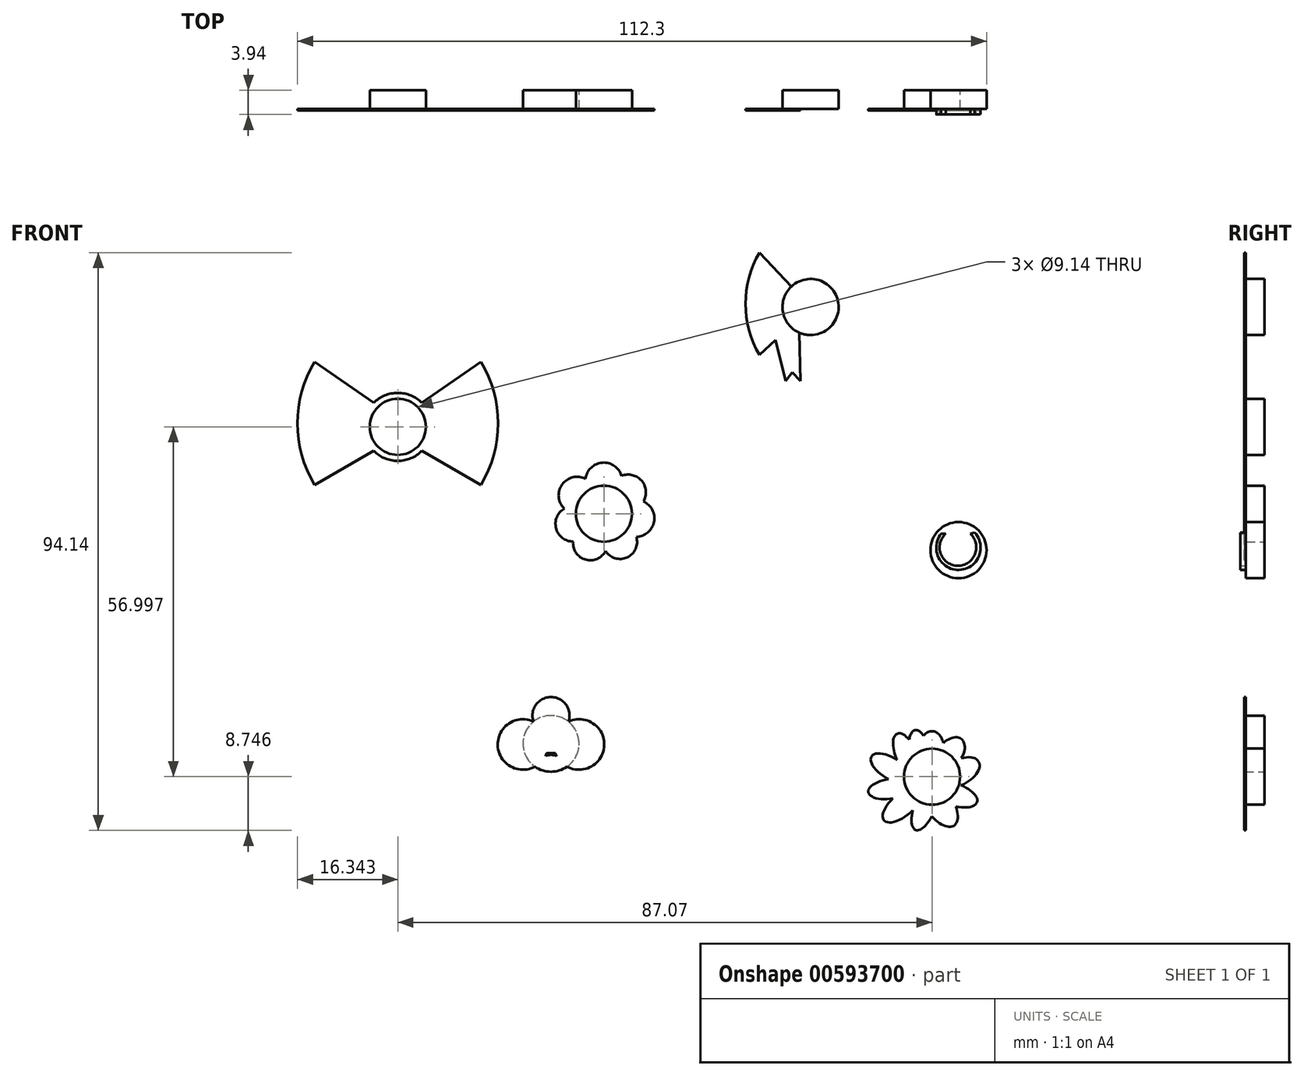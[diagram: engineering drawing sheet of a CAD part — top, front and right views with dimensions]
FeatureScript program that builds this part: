
annotation { "Feature Type Name" : "Feature", "Feature Type Description" : "" }
export const myFeature = defineFeature(function(context is Context, id is Id, definition is map)
    precondition{}
    {
        {
            var Q0;
            Q0=qCreatedBy(makeId("Front.planeOp"),FACE);
            var sketch = newSketch(context, id + "F0", { "sketchPlane" : qUnion([Q0])});
            skCircle(sketch, "E0", {"center": v(-50.12, 43.15) * mm, "radius": 4.57 * mm});
            skCircle(sketch, "E1", {"center": v(-16.53, 29) * mm, "radius": 4.57 * mm});
            skCircle(sketch, "E2", {"center": v(41.26, 23.07) * mm, "radius": 4.57 * mm});
            skCircle(sketch, "E3", {"center": v(17.15, 62.68) * mm, "radius": 4.57 * mm});
            skCircle(sketch, "E4", {"center": v(-25.15, -8.45) * mm, "radius": 4.57 * mm});
            skCircle(sketch, "E5", {"center": v(36.95, -13.84) * mm, "radius": 4.57 * mm});
            skSolve(sketch);
        }
        {
            var Q0;
            Q0=makeQuery(id+"F0.imprint","IMPRINT",FACE,{"disambiguationData":[TD([[makeQuery(id+"F0.imprint","IMPRINT",EDGE,{"derivedFrom":sQuery(id+"F0.wireOp",EDGE,"E0")}),1.0]])]});
            var Q1;
            Q1=makeQuery(id+"F0.imprint","IMPRINT",FACE,{"disambiguationData":[TD([[makeQuery(id+"F0.imprint","IMPRINT",EDGE,{"derivedFrom":sQuery(id+"F0.wireOp",EDGE,"E1")}),1.0]])]});
            var Q2;
            Q2=makeQuery(id+"F0.imprint","IMPRINT",FACE,{"disambiguationData":[TD([[makeQuery(id+"F0.imprint","IMPRINT",EDGE,{"derivedFrom":sQuery(id+"F0.wireOp",EDGE,"E3")}),1.0]])]});
            var Q3;
            Q3=makeQuery(id+"F0.imprint","IMPRINT",FACE,{"disambiguationData":[TD([[makeQuery(id+"F0.imprint","IMPRINT",EDGE,{"derivedFrom":sQuery(id+"F0.wireOp",EDGE,"E2")}),1.0]])]});
            var Q4;
            Q4=makeQuery(id+"F0.imprint","IMPRINT",FACE,{"disambiguationData":[TD([[makeQuery(id+"F0.imprint","IMPRINT",EDGE,{"derivedFrom":sQuery(id+"F0.wireOp",EDGE,"E4")}),1.0]])]});
            var Q5;
            Q5=makeQuery(id+"F0.imprint","IMPRINT",FACE,{"disambiguationData":[TD([[makeQuery(id+"F0.imprint","IMPRINT",EDGE,{"derivedFrom":sQuery(id+"F0.wireOp",EDGE,"E5")}),1.0]])]});
            extrude(context, id + "F1", {"entities" : qUnion([Q0, Q1, Q2, Q3, Q4, Q5]), "depth" : 3.05 * mm, "offsetDistance" : 25.4 * mm});
        }
        {
            var Q0;
            Q0=makeQuery(id+"F1.opExtrude","CAP_FACE",FACE,{"disambiguationData":[OSD([sQuery(id+"F0.wireOp",EDGE,"E0")])],"isStart":false});
            var sketch = newSketch(context, id + "F2", { "sketchPlane" : qUnion([Q0])});
            skCircle(sketch, "E6", {"center": v(-50.12, 43.15) * mm, "radius": 5.54 * mm});
            skLineSegment(sketch, "E7", {"start": v(-46.2, 47.06) * mm, "end": v(-36.57, 53.77) * mm});
            skLineSegment(sketch, "E8", {"start": v(-46.2, 39.24) * mm, "end": v(-36.57, 33.68) * mm});
            skArc(sketch, "E9", {"start": v(-36.57, 33.68) * mm, "mid": v(-33.77, 43.73) * mm, "end": v(-36.57, 53.77) * mm});
            skLineSegment(sketch, "E10.MirrorCS", {"start": v(-54.04, 47.06) * mm, "end": v(-63.67, 53.77) * mm});
            skLineSegment(sketch, "E11.MirrorCS", {"start": v(-54.04, 39.24) * mm, "end": v(-63.67, 33.68) * mm});
            skArc(sketch, "E12.MirrorCS", {"start": v(-63.67, 33.68) * mm, "mid": v(-66.46, 43.73) * mm, "end": v(-63.67, 53.77) * mm});
            skSolve(sketch);
        }
        {
            var Q0;
            Q0=makeQuery(id+"F2.imprint","IMPRINT",FACE,{"disambiguationData":[TD([[makeQuery(id+"F2.imprint","IMPRINT",EDGE,{"derivedFrom":makeQuery(id+"F1.opExtrude","CAP_EDGE",EDGE,{"disambiguationData":[OSD([sQuery(id+"F0.wireOp",EDGE,"E0")])],"isStart":false})}),-1.0]])]});
            extrude(context, id + "F3", {"entities" : qUnion([Q0]), "depth" : 0.25 * mm, "offsetDistance" : 25.4 * mm});
        }
        {
            var Q0;
            {var subQ0=sQuery(id+"F2.wireOp",EDGE,"E10.MirrorCS");Q0=makeQuery(id+"F2.imprint","IMPRINT",FACE,{"disambiguationData":[TD([[makeQuery(id+"F2.imprint","IMPRINT",EDGE,{"derivedFrom":subQ0}),1.0]])]});}
            var Q1;
            {var subQ0=sQuery(id+"F2.wireOp",EDGE,"E7");Q1=makeQuery(id+"F2.imprint","IMPRINT",FACE,{"disambiguationData":[TD([[makeQuery(id+"F2.imprint","IMPRINT",EDGE,{"derivedFrom":subQ0}),-1.0]])]});}
            extrude(context, id + "F4", {"entities" : qUnion([Q0, Q1]), "operationType" : NewBodyOperationType.ADD, "depth" : 0.25 * mm, "offsetDistance" : 25.4 * mm});
        }
        {
            var Q0;
            Q0=makeQuery(id+"F1.opExtrude","CAP_FACE",FACE,{"disambiguationData":[OSD([sQuery(id+"F0.wireOp",EDGE,"E1")])],"isStart":false});
            var sketch = newSketch(context, id + "F5", { "sketchPlane" : qUnion([Q0])});
            skArc(sketch, "E13", {"start": v(-17.86, 31.63) * mm, "mid": v(-16.6, 31.33) * mm, "end": v(-15.32, 31.58) * mm});
            skArc(sketch, "E14", {"start": v(-19.53, 34.7) * mm, "mid": v(-23.34, 33.75) * mm, "end": v(-23, 29.83) * mm});
            skArc(sketch, "E15", {"start": v(-23, 29.83) * mm, "mid": v(-24.32, 26.6) * mm, "end": v(-21.54, 24.47) * mm});
            skArc(sketch, "E16", {"start": v(-21.54, 24.47) * mm, "mid": v(-19.54, 21.53) * mm, "end": v(-16.26, 22.93) * mm});
            skArc(sketch, "E17", {"start": v(-16.26, 22.93) * mm, "mid": v(-12.75, 21.89) * mm, "end": v(-11.24, 25.24) * mm});
            skArc(sketch, "E18", {"start": v(-11.24, 25.24) * mm, "mid": v(-8.37, 27.65) * mm, "end": v(-10.1, 30.99) * mm});
            skArc(sketch, "E19", {"start": v(-10.1, 30.99) * mm, "mid": v(-10.37, 34.36) * mm, "end": v(-13.66, 35.17) * mm});
            skArc(sketch, "E20.trimOffspring", {"start": v(-19.44, 29.32) * mm, "mid": v(-18.37, 30.28) * mm, "end": v(-17.86, 31.63) * mm});
            skArc(sketch, "E21.trimOffspring", {"start": v(-18.68, 27.01) * mm, "mid": v(-18.8, 28.25) * mm, "end": v(-19.44, 29.32) * mm});
            skPoint(sketch, "E22.center.orphan", {"position": v(-16.53, 29) * mm});
            skArc(sketch, "E23.trimOffspring", {"start": v(-16.38, 25.7) * mm, "mid": v(-17.37, 26.65) * mm, "end": v(-18.68, 27.01) * mm});
            skArc(sketch, "E24.trimOffspring", {"start": v(-14.13, 27.2) * mm, "mid": v(-15.45, 26.74) * mm, "end": v(-16.38, 25.7) * mm});
            skArc(sketch, "E25.trimOffspring", {"start": v(-13.83, 29.88) * mm, "mid": v(-14.3, 28.57) * mm, "end": v(-14.13, 27.2) * mm});
            skArc(sketch, "E26.trimOffspring", {"start": v(-15.32, 31.58) * mm, "mid": v(-14.75, 30.58) * mm, "end": v(-13.83, 29.88) * mm});
            skArc(sketch, "E27.trimOffspring", {"start": v(-13.66, 35.17) * mm, "mid": v(-16.78, 37.32) * mm, "end": v(-19.53, 34.7) * mm});
            skSolve(sketch);
        }
        {
            var Q0;
            Q0=makeQuery(id+"F5.imprint","IMPRINT",FACE,{"disambiguationData":[TD([[makeQuery(id+"F5.imprint","IMPRINT",EDGE,{"derivedFrom":sQuery(id+"F5.wireOp",EDGE,"E14")}),1.0]])]});
            extrude(context, id + "F6", {"entities" : qUnion([Q0]), "depth" : 0.25 * mm, "offsetDistance" : 25.4 * mm});
        }
        {
            var Q0;
            Q0=makeQuery(id+"F1.opExtrude","CAP_FACE",FACE,{"disambiguationData":[OSD([sQuery(id+"F0.wireOp",EDGE,"E3")])],"isStart":false});
            var sketch = newSketch(context, id + "F7", { "sketchPlane" : qUnion([Q0])});
            skLineSegment(sketch, "E28", {"start": v(17.15, 62.68) * mm, "end": v(8.82, 71.55) * mm});
            skLineSegment(sketch, "E29", {"start": v(17.15, 62.68) * mm, "end": v(15.24, 60.88) * mm});
            skArc(sketch, "E30", {"start": v(8.82, 71.55) * mm, "mid": v(6.56, 63.2) * mm, "end": v(8.82, 54.86) * mm});
            skLineSegment(sketch, "E31.MirrorCS", {"start": v(17.15, 62.68) * mm, "end": v(25.48, 71.55) * mm});
            skArc(sketch, "E32.MirrorCS", {"start": v(25.48, 71.55) * mm, "mid": v(27.74, 63.2) * mm, "end": v(25.48, 54.86) * mm});
            skLineSegment(sketch, "E33.MirrorCS", {"start": v(17.15, 62.68) * mm, "end": v(19.06, 60.88) * mm});
            skLineSegment(sketch, "E34", {"start": v(15.47, 50.66) * mm, "end": v(14.16, 52.05) * mm});
            skLineSegment(sketch, "E35", {"start": v(14.16, 52.05) * mm, "end": v(13.1, 50.66) * mm});
            skLineSegment(sketch, "E36", {"start": v(13.1, 50.66) * mm, "end": v(11.44, 57.32) * mm});
            skLineSegment(sketch, "E37", {"start": v(15.47, 50.66) * mm, "end": v(15.24, 60.88) * mm});
            skLineSegment(sketch, "E38.trimOffspring", {"start": v(11.44, 57.32) * mm, "end": v(8.82, 54.86) * mm});
            skLineSegment(sketch, "E39.MirrorCS", {"start": v(21.2, 50.66) * mm, "end": v(22.86, 57.32) * mm});
            skLineSegment(sketch, "E40.MirrorCS", {"start": v(18.83, 50.66) * mm, "end": v(19.06, 60.88) * mm});
            skLineSegment(sketch, "E41.MirrorCS", {"start": v(18.83, 50.66) * mm, "end": v(20.14, 52.05) * mm});
            skLineSegment(sketch, "E42.MirrorCS", {"start": v(20.14, 52.05) * mm, "end": v(21.2, 50.66) * mm});
            skLineSegment(sketch, "E43.trimOffspring", {"start": v(22.86, 57.32) * mm, "end": v(25.48, 54.86) * mm});
            skSolve(sketch);
        }
        {
            var Q0;
            {var subQ0=sQuery(id+"F7.wireOp",EDGE,"E30");Q0=makeQuery(id+"F7.imprint","IMPRINT",FACE,{"disambiguationData":[TD([[makeQuery(id+"F7.imprint","IMPRINT",EDGE,{"derivedFrom":subQ0}),1.0]])]});}
            var Q1;
            {var subQ0=sQuery(id+"F7.wireOp",EDGE,"E32.MirrorCS");Q1=makeQuery(id+"F7.imprint","IMPRINT",FACE,{"disambiguationData":[TD([[makeQuery(id+"F7.imprint","IMPRINT",EDGE,{"derivedFrom":subQ0}),-1.0]])]});}
            extrude(context, id + "F8", {"entities" : qUnion([Q0, Q1]), "depth" : 0.25 * mm, "offsetDistance" : 25.4 * mm});
        }
        {
            var Q0;
            Q0=makeQuery(id+"F1.opExtrude","CAP_FACE",FACE,{"disambiguationData":[OSD([sQuery(id+"F0.wireOp",EDGE,"E4")])],"isStart":false});
            var sketch = newSketch(context, id + "F9", { "sketchPlane" : qUnion([Q0])});
            skArc(sketch, "E44", {"start": v(-25.76, -7.48) * mm, "mid": v(-25.88, -7.12) * mm, "end": v(-26.03, -6.77) * mm});
            skArc(sketch, "E45.MirrorC", {"start": v(-24.55, -7.48) * mm, "mid": v(-24.43, -7.12) * mm, "end": v(-24.27, -6.77) * mm});
            skLineSegment(sketch, "E46.bottom", {"start": v(-25.76, -7.48) * mm, "end": v(-24.55, -7.48) * mm});
            skLineSegment(sketch, "E46.top", {"start": v(-25.86, -10) * mm, "end": v(-24.45, -10) * mm});
            skArc(sketch, "E47", {"start": v(-26.03, -6.77) * mm, "mid": v(-25.15, -6.9) * mm, "end": v(-24.27, -6.77) * mm});
            skPoint(sketch, "E47.centerSnap0", {"position": v(-25.15, -7.48) * mm});
            skArc(sketch, "E48", {"start": v(-27.76, -12.2) * mm, "mid": v(-25.15, -15.76) * mm, "end": v(-22.55, -12.2) * mm});
            skPoint(sketch, "E48.centerSnap0", {"position": v(-25.15, -10) * mm});
            skArc(sketch, "E49.trimOffspring", {"start": v(-28.02, -4.85) * mm, "mid": v(-33.83, -8.73) * mm, "end": v(-27.76, -12.2) * mm});
            skArc(sketch, "E50.trimOffspring", {"start": v(-22.29, -4.85) * mm, "mid": v(-16.47, -8.73) * mm, "end": v(-22.55, -12.2) * mm});
            skArc(sketch, "E51.trimOffspring", {"start": v(-22.29, -4.85) * mm, "mid": v(-25.15, -0.86) * mm, "end": v(-28.02, -4.85) * mm});
            skArc(sketch, "E52.trimOffspring", {"start": v(-26.05, -10.44) * mm, "mid": v(-25.95, -10.22) * mm, "end": v(-25.86, -10) * mm});
            skArc(sketch, "E53.trimOffspring", {"start": v(-24.25, -10.44) * mm, "mid": v(-25.15, -10.3) * mm, "end": v(-26.05, -10.44) * mm});
            skArc(sketch, "E54.trimOffspring", {"start": v(-24.25, -10.44) * mm, "mid": v(-24.36, -10.22) * mm, "end": v(-24.45, -10) * mm});
            skSolve(sketch);
        }
        {
            var Q0;
            {var subQ0=sQuery(id+"F9.wireOp",EDGE,"E45.MirrorC");var subQ1=makeQuery(id+"F1.opExtrude","CAP_EDGE",EDGE,{"disambiguationData":[OSD([sQuery(id+"F0.wireOp",EDGE,"E4")])],"isStart":false});var subQ2=makeQuery(id+"F9.imprint","INTERSECT",VERTEX,{"disambiguationData":[OD(0.0)],"derivedFrom":[subQ1,subQ0]});Q0=makeQuery(id+"F9.imprint","IMPRINT",FACE,{"disambiguationData":[TD([[makeQuery(id+"F9.imprint","IMPRINT",EDGE,{"disambiguationData":[TD([[subQ2,-1.0]])],"derivedFrom":subQ0}),-1.0]])]});}
            var Q1;
            {var subQ0=sQuery(id+"F9.wireOp",EDGE,"E46.bottom");Q1=makeQuery(id+"F9.imprint","IMPRINT",FACE,{"disambiguationData":[TD([[makeQuery(id+"F9.imprint","IMPRINT",EDGE,{"derivedFrom":subQ0}),-1.0]])]});}
            var Q2;
            {var subQ0=sQuery(id+"F9.wireOp",EDGE,"E44");var subQ1=makeQuery(id+"F1.opExtrude","CAP_EDGE",EDGE,{"disambiguationData":[OSD([sQuery(id+"F0.wireOp",EDGE,"E4")])],"isStart":false});var subQ2=makeQuery(id+"F9.imprint","INTERSECT",VERTEX,{"disambiguationData":[OD(0.0)],"derivedFrom":[subQ1,subQ0]});Q2=makeQuery(id+"F9.imprint","IMPRINT",FACE,{"disambiguationData":[TD([[makeQuery(id+"F9.imprint","IMPRINT",EDGE,{"disambiguationData":[TD([[subQ2,-1.0]])],"derivedFrom":subQ0}),1.0]])]});}
            extrude(context, id + "F10", {"entities" : qUnion([Q0, Q1, Q2]), "operationType" : NewBodyOperationType.ADD, "depth" : 0.25 * mm, "offsetDistance" : 25.4 * mm});
        }
        {
            var Q0;
            {var subQ0=sQuery(id+"F9.wireOp",EDGE,"E51.trimOffspring");Q0=makeQuery(id+"F9.imprint","IMPRINT",FACE,{"disambiguationData":[TD([[makeQuery(id+"F9.imprint","IMPRINT",EDGE,{"derivedFrom":subQ0}),1.0]])]});}
            extrude(context, id + "F11", {"entities" : qUnion([Q0]), "operationType" : NewBodyOperationType.ADD, "depth" : 0.25 * mm, "offsetDistance" : 25.4 * mm});
        }
        {
            var Q0;
            {var subQ0=sQuery(id+"F9.wireOp",EDGE,"E48");var subQ1=makeQuery(id+"F1.opExtrude","CAP_EDGE",EDGE,{"disambiguationData":[OSD([sQuery(id+"F0.wireOp",EDGE,"E4")])],"isStart":false});var subQ2=makeQuery(id+"F9.imprint","INTERSECT",VERTEX,{"disambiguationData":[OD(0.0)],"derivedFrom":[subQ1,subQ0]});Q0=makeQuery(id+"F9.imprint","IMPRINT",FACE,{"disambiguationData":[TD([[makeQuery(id+"F9.imprint","IMPRINT",EDGE,{"disambiguationData":[TD([[subQ2,-1.0]])],"derivedFrom":subQ0}),1.0]])]});}
            extrude(context, id + "F12", {"entities" : qUnion([Q0]), "operationType" : NewBodyOperationType.ADD, "depth" : 0.25 * mm, "offsetDistance" : 25.4 * mm});
        }
        {
            var Q0;
            Q0=makeQuery(id+"F1.opExtrude","CAP_FACE",FACE,{"disambiguationData":[OSD([sQuery(id+"F0.wireOp",EDGE,"E2")])],"isStart":false});
            var sketch = newSketch(context, id + "F13", { "sketchPlane" : qUnion([Q0])});
            skArc(sketch, "E55", {"start": v(38.45, 25.75) * mm, "mid": v(41.37, 19.85) * mm, "end": v(43.9, 25.92) * mm});
            skLineSegment(sketch, "E56", {"start": v(38.45, 25.75) * mm, "end": v(39.17, 25.75) * mm});
            skLineSegment(sketch, "E57", {"start": v(43.17, 25.75) * mm, "end": v(43.9, 25.92) * mm});
            skArc(sketch, "E58", {"start": v(39.17, 25.75) * mm, "mid": v(41.17, 20.52) * mm, "end": v(43.17, 25.75) * mm});
            skSolve(sketch);
        }
        {
            var Q0;
            Q0=makeQuery(id+"F13.imprint","IMPRINT",FACE,{"disambiguationData":[TD([[makeQuery(id+"F13.imprint","IMPRINT",EDGE,{"derivedFrom":sQuery(id+"F13.wireOp",EDGE,"E55")}),1.0]])]});
            extrude(context, id + "F14", {"entities" : qUnion([Q0]), "operationType" : NewBodyOperationType.ADD, "depth" : 0.89 * mm, "offsetDistance" : 25.4 * mm});
        }
        {
            var Q0;
            Q0=makeQuery(id+"F1.opExtrude","CAP_FACE",FACE,{"disambiguationData":[OSD([sQuery(id+"F0.wireOp",EDGE,"E5")])],"isStart":false});
            var sketch = newSketch(context, id + "F15", { "sketchPlane" : qUnion([Q0])});
            skEllipticalArc(sketch, "E59", {});
            skEllipticalArc(sketch, "E60", {});
            skEllipticalArc(sketch, "E61.MirrorC", {});
            skEllipticalArc(sketch, "E62.MirrorC", {});
            skEllipticalArc(sketch, "E63.MirrorC", {});
            skEllipticalArc(sketch, "E64", {});
            skEllipticalArc(sketch, "E65", {});
            skEllipticalArc(sketch, "E66.trimOffspring", {});
            skEllipticalArc(sketch, "E67.trimOffspring", {});
            skEllipticalArc(sketch, "E68", {});
            skEllipticalArc(sketch, "E69", {});
            skCircle(sketch, "E70", {"center": v(36.95, -13.84) * mm, "radius": 4.92 * mm});
            const initialGuessF15  = {"E59": [0.03689506488513964, -0.009272064358855211, 0, -1, 0.0028529701561523105, 0.0019932729329459856, 1.8962791895681808, 3.880474591508582], "E60": [0.04049271924061474, -0.016738259848719583, 0.9513302794306697, -0.3081731646953771, 0.003978370025130945, 0.0018120636768992632, 4.945305681299697, 1.405893599911402], "E61.MirrorC": [0.03017371805998067, -0.012443225906584296, -0.8515373360237825, 0.524293968454263, 0.0036248144871330575, 0.0017237005556510932, 4.659023526756916, 1.765837926804689], "E62.MirrorC": [0.029998623459039697, -0.015847459880857243, -0.9891605863523939, -0.14683778262759362, 0.003474473086800068, 0.0015962673350098276, 4.6771836116898715, 1.6709761124408802], "E63.MirrorC": [0.03215018751682465, -0.018385949722934808, -0.7627363868443588, -0.6467095207151452, 0.003978370025130945, 0.0018120636768992632, 4.849144724791033, 1.7266244163154105], "E64": [0.035916102664716176, -0.01829639206294132, -0.35876713816905287, -0.9334270944053359, 0.004549739517657043, 0.001751362723647701, 5.107716065873097, 1.2373857722322668], "E65": [0.038142087968877206, -0.018258540968928594, 0.558114356894791, -0.8297640415370587, 0.004282066143164985, 0.0021973513663687714, 4.947848665173196, 1.1211086162269435], "E66.trimOffspring": [0.03263920967194804, -0.010112616096993057, 0.38017946289027, -0.924912739666, 0.0035473310419283396, 0.0016694837575602346, 2.142308031215101, 4.814636394461722], "E67.trimOffspring": [0.03480405274624054, -0.009808568737273884, 0.15799607510086647, -0.9874397400614994, 0.0036035588237469107, 0.0016031714825985657, 2.3351725788401554, 4.0446381263319875], "E68": [0.039765888114950236, -0.010238858790041949, -0.6100537294341276, -0.7923600489698559, 0.003198779592693337, 0.002003661586314592, 1.8004304811878924, 4.430531625774407], "E69": [0.04146920110907196, -0.013127129810640207, -0.8708229333608337, -0.4915968050474219, 0.003522641966378256, 0.001996824267462396, 1.3218793151524226, 4.313516207494243]};
            skSetInitialGuess(sketch, initialGuessF15);
            skSolve(sketch);
        }
        {
            var Q0;
            Q0=makeQuery(id+"F15.imprint","IMPRINT",FACE,{"disambiguationData":[TD([[makeQuery(id+"F15.imprint","IMPRINT",EDGE,{"derivedFrom":makeQuery(id+"F1.opExtrude","CAP_EDGE",EDGE,{"disambiguationData":[OSD([sQuery(id+"F0.wireOp",EDGE,"E5")])],"isStart":false})}),-1.0]])]});
            extrude(context, id + "F16", {"entities" : qUnion([Q0]), "depth" : 0.25 * mm, "offsetDistance" : 25.4 * mm});
        }
        {
            var Q0;
            Q0=makeQuery(id+"F15.imprint","IMPRINT",FACE,{"disambiguationData":[TD([[makeQuery(id+"F15.imprint","IMPRINT",EDGE,{"derivedFrom":sQuery(id+"F15.wireOp",EDGE,"E59")}),1.0]])]});
            extrude(context, id + "F17", {"entities" : qUnion([Q0]), "operationType" : NewBodyOperationType.ADD, "depth" : 0.25 * mm, "offsetDistance" : 25.4 * mm});
        }
    });
